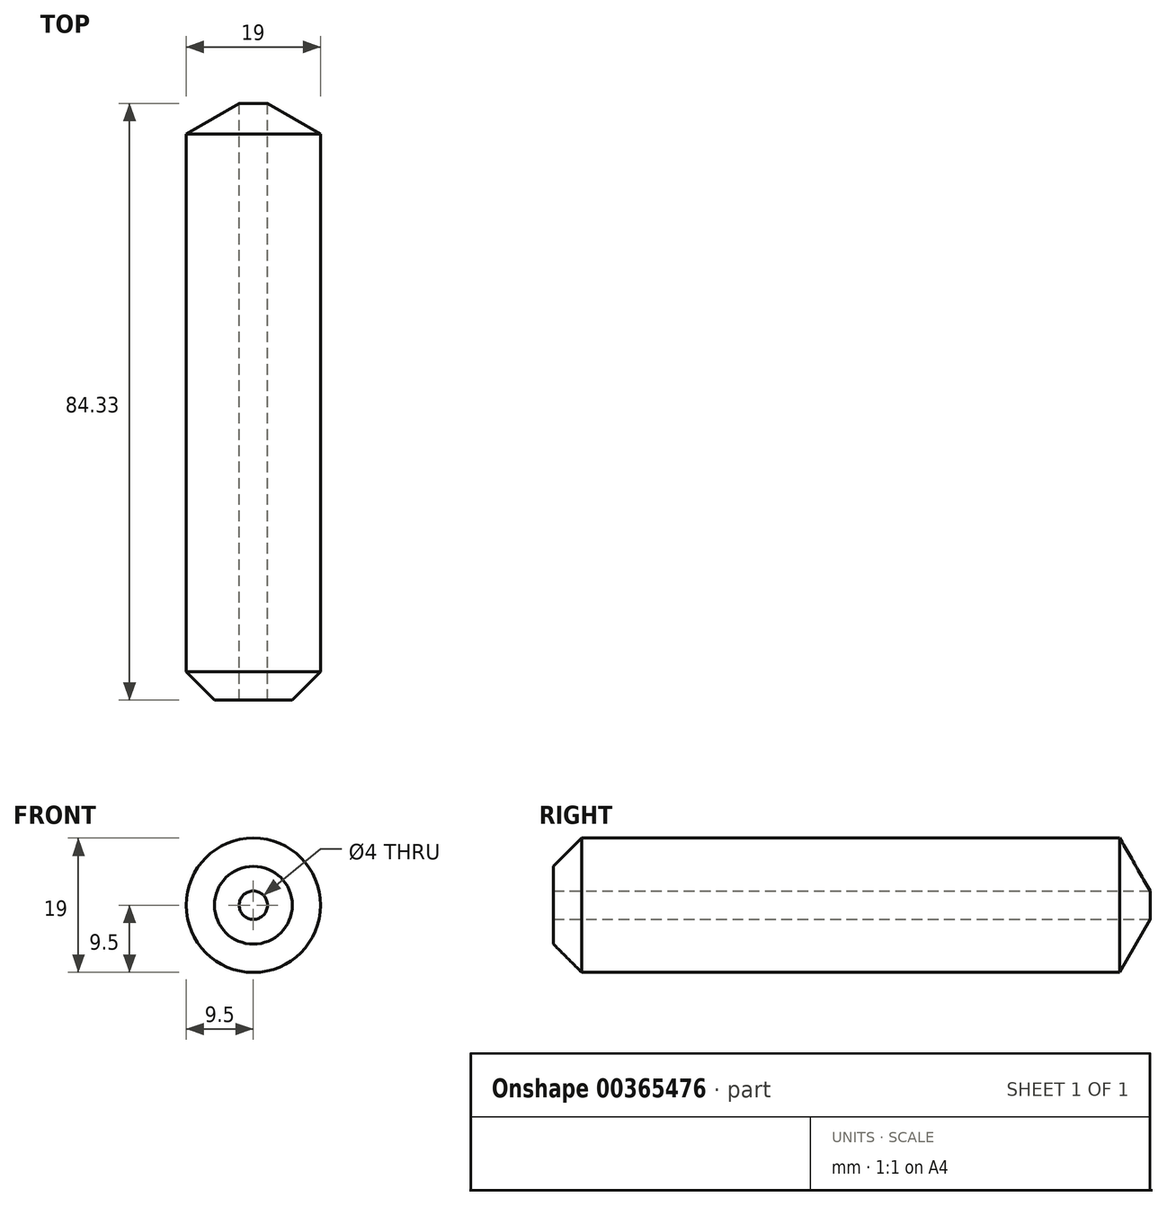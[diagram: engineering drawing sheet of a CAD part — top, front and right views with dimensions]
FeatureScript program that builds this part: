
annotation { "Feature Type Name" : "Feature", "Feature Type Description" : "" }
export const myFeature = defineFeature(function(context is Context, id is Id, definition is map)
    precondition{}
    {
        {
            var Q0;
            Q0=qCreatedBy(makeId("Front.planeOp"),FACE);
            var sketch = newSketch(context, id + "F0", { "sketchPlane" : qUnion([Q0])});
            skCircle(sketch, "E0", {"center": v(0, 0) * mm, "radius": 9.5 * mm});
            skCircle(sketch, "E1", {"center": v(0, 0) * mm, "radius": 2 * mm});
            skSolve(sketch);
        }
        {
            var Q0;
            Q0 = qSketchRegion(id + "F0", true);
            extrude(context, id + "F1", {"entities" : qUnion([Q0]), "depth" : 80 * mm});
        }
        {
            var Q0;
            Q0=makeQuery(id+"F1.opExtrude","CAP_FACE",FACE,{"disambiguationData":[OSD([sQuery(id+"F0.wireOp",EDGE,"E0"),sQuery(id+"F0.wireOp",EDGE,"E1")])],"isStart":true});
            var sketch = newSketch(context, id + "F2", { "sketchPlane" : qUnion([Q0])});
            skCircle(sketch, "E2", {"center": v(0, 0) * mm, "radius": 9.5 * mm});
            skSolve(sketch);
        }
        {
            var Q0;
            Q0 = qSketchRegion(id + "F2", true);
            extrude(context, id + "F3", {"entities" : qUnion([Q0]), "operationType" : NewBodyOperationType.ADD, "depth" : 5 * mm, "hasDraft" : true, "draftAngle" : 60 * degree, "draftPullDirection" : true});
        }
        {
            var Q0;
            Q0=makeQuery(id+"F3.opExtrude","CAP_FACE",FACE,{"disambiguationData":[OSD([sQuery(id+"F2.wireOp",EDGE,"E2")])],"isStart":false});
            var sketch = newSketch(context, id + "F4", { "sketchPlane" : qUnion([Q0])});
            skCircle(sketch, "E3", {"center": v(0, 0) * mm, "radius": 2 * mm});
            skSolve(sketch);
        }
        {
            var Q0;
            Q0 = qSketchRegion(id + "F4", true);
            extrude(context, id + "F5", {"entities" : qUnion([Q0]), "operationType" : NewBodyOperationType.REMOVE, "oppositeDirection" : true, "depth" : 25 * mm});
        }
        {
            var Q0;
            Q0=makeQuery(id+"F1.opExtrude","CAP_EDGE",EDGE,{"disambiguationData":[OSD([sQuery(id+"F0.wireOp",EDGE,"E0")])],"isStart":false});
            chamfer(context, id + "F6", {"entities" : qUnion([Q0]), "width" : 4 * mm, "tangentPropagation" : true});
        }
    });
